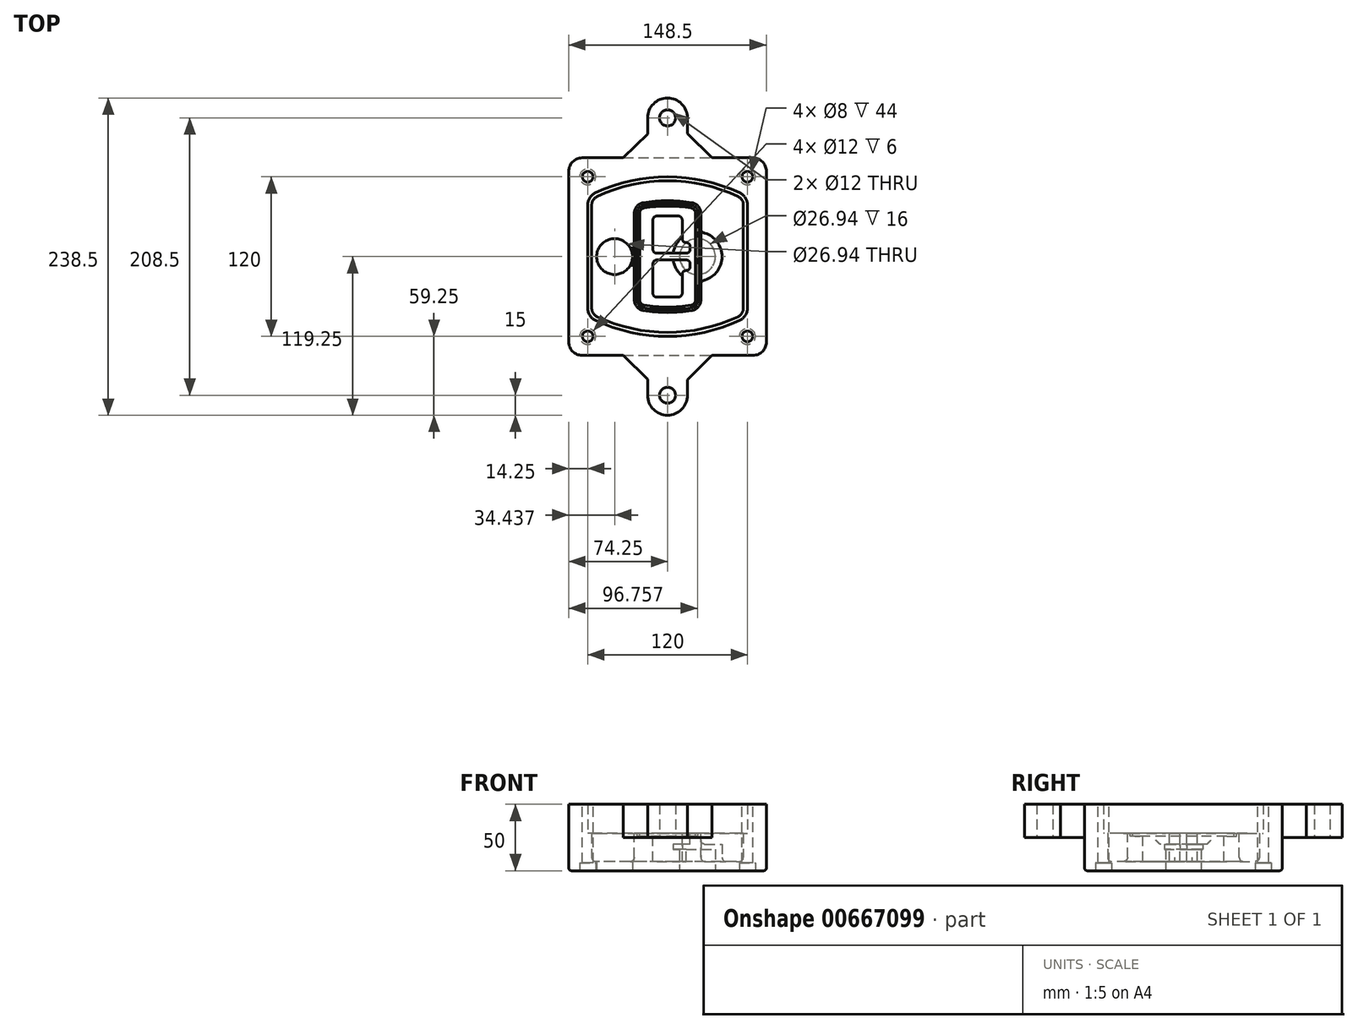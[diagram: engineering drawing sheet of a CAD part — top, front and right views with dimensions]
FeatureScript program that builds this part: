
annotation { "Feature Type Name" : "Feature", "Feature Type Description" : "" }
export const myFeature = defineFeature(function(context is Context, id is Id, definition is map)
    precondition{}
    {
        {
            var Q0;
            Q0=qCreatedBy(makeId("Top.planeOp"),FACE);
            var sketch = newSketch(context, id + "F0", { "sketchPlane" : qUnion([Q0])});
            skPoint(sketch, "E0.rect.middle", {"position": v(0, 0) * mm});
            skLineSegment(sketch, "E1.bottom", {"start": v(-64.25, -74.25) * mm, "end": v(64.25, -74.25) * mm});
            skLineSegment(sketch, "E1.top", {"start": v(-64.25, 74.25) * mm, "end": v(64.25, 74.25) * mm});
            skLineSegment(sketch, "E1.left", {"start": v(-74.25, -64.25) * mm, "end": v(-74.25, 64.25) * mm});
            skLineSegment(sketch, "E1.right", {"start": v(74.25, -64.25) * mm, "end": v(74.25, 64.25) * mm});
            skLineSegment(sketch, "E2", {"start": v(-74.25, 74.25) * mm, "end": v(74.25, -74.25) * mm, "construction": true});
            skLineSegment(sketch, "E3", {"start": v(74.25, 74.25) * mm, "end": v(-74.25, -74.25) * mm, "construction": true});
            skCircle(sketch, "E4", {"center": v(-60, 60) * mm, "radius": 4 * mm});
            skCircle(sketch, "E5", {"center": v(60, 60) * mm, "radius": 4 * mm});
            skCircle(sketch, "E6", {"center": v(60, -60) * mm, "radius": 4 * mm});
            skCircle(sketch, "E7", {"center": v(-60, -60) * mm, "radius": 4 * mm});
            skLineSegment(sketch, "E8", {"start": v(-60, 60) * mm, "end": v(60, 60) * mm, "construction": true});
            skLineSegment(sketch, "E9", {"start": v(60, 60) * mm, "end": v(60, -60) * mm, "construction": true});
            skLineSegment(sketch, "E10", {"start": v(60, -60) * mm, "end": v(-60, -60) * mm, "construction": true});
            skLineSegment(sketch, "E11", {"start": v(-60, -60) * mm, "end": v(-60, 60) * mm, "construction": true});
            skLineSegment(sketch, "E12", {"start": v(-60, 38.83) * mm, "end": v(-60, -38.83) * mm});
            skLineSegment(sketch, "E13", {"start": v(60, 38.83) * mm, "end": v(60, -38.83) * mm});
            skArc(sketch, "E14", {"start": v(54.26, 47.88) * mm, "mid": v(0, 60) * mm, "end": v(-54.26, 47.88) * mm});
            skArc(sketch, "E15", {"start": v(-54.26, -47.88) * mm, "mid": v(0, -60) * mm, "end": v(54.26, -47.88) * mm});
            skLineSegment(sketch, "E16", {"start": v(-60, 0) * mm, "end": v(60, 0) * mm, "construction": true});
            skPoint(sketch, "E17.visualSharp", {"position": v(-60, -45) * mm});
            skArc(sketch, "E17.filletArc", {"start": v(-60, -38.83) * mm, "mid": v(-58.44, -44.2) * mm, "end": v(-54.26, -47.88) * mm});
            skPoint(sketch, "E18.visualSharp", {"position": v(-60, 45) * mm});
            skArc(sketch, "E18.filletArc", {"start": v(-54.26, 47.88) * mm, "mid": v(-58.44, 44.2) * mm, "end": v(-60, 38.83) * mm});
            skPoint(sketch, "E19.visualSharp", {"position": v(60, 45) * mm});
            skArc(sketch, "E19.filletArc", {"start": v(60, 38.83) * mm, "mid": v(58.44, 44.2) * mm, "end": v(54.26, 47.88) * mm});
            skPoint(sketch, "E20.visualSharp", {"position": v(60, -45) * mm});
            skArc(sketch, "E20.filletArc", {"start": v(54.26, -47.88) * mm, "mid": v(58.44, -44.2) * mm, "end": v(60, -38.83) * mm});
            skPoint(sketch, "E21.visualSharp", {"position": v(-74.25, 74.25) * mm});
            skArc(sketch, "E21.filletArc", {"start": v(-64.25, 74.25) * mm, "mid": v(-71.32, 71.32) * mm, "end": v(-74.25, 64.25) * mm});
            skPoint(sketch, "E22.visualSharp", {"position": v(74.25, 74.25) * mm});
            skArc(sketch, "E22.filletArc", {"start": v(74.25, 64.25) * mm, "mid": v(71.32, 71.32) * mm, "end": v(64.25, 74.25) * mm});
            skPoint(sketch, "E23.visualSharp", {"position": v(74.25, -74.25) * mm});
            skArc(sketch, "E23.filletArc", {"start": v(64.25, -74.25) * mm, "mid": v(71.32, -71.32) * mm, "end": v(74.25, -64.25) * mm});
            skPoint(sketch, "E24.visualSharp", {"position": v(-74.25, -74.25) * mm});
            skArc(sketch, "E24.filletArc", {"start": v(-74.25, -64.25) * mm, "mid": v(-71.32, -71.32) * mm, "end": v(-64.25, -74.25) * mm});
            skArc(sketch, "E25.0", {"start": v(57, 38.83) * mm, "mid": v(55.9, 42.58) * mm, "end": v(52.98, 45.17) * mm});
            skLineSegment(sketch, "E25.1", {"start": v(57, 38.83) * mm, "end": v(57, -38.83) * mm});
            skArc(sketch, "E25.2", {"start": v(52.98, -45.17) * mm, "mid": v(55.9, -42.58) * mm, "end": v(57, -38.83) * mm});
            skArc(sketch, "E25.3", {"start": v(-52.98, -45.17) * mm, "mid": v(0, -57) * mm, "end": v(52.98, -45.17) * mm});
            skArc(sketch, "E25.4", {"start": v(-57, -38.83) * mm, "mid": v(-55.9, -42.58) * mm, "end": v(-52.98, -45.17) * mm});
            skArc(sketch, "E25.5", {"start": v(52.98, 45.17) * mm, "mid": v(0, 57) * mm, "end": v(-52.98, 45.17) * mm});
            skLineSegment(sketch, "E25.6", {"start": v(-57, 38.83) * mm, "end": v(-57, -38.83) * mm});
            skArc(sketch, "E25.7", {"start": v(-52.98, 45.17) * mm, "mid": v(-55.9, 42.58) * mm, "end": v(-57, 38.83) * mm});
            skArc(sketch, "E26.0", {"start": v(-55.96, 51.5) * mm, "mid": v(-61.82, 46.33) * mm, "end": v(-64, 38.83) * mm});
            skArc(sketch, "E26.1", {"start": v(55.96, 51.5) * mm, "mid": v(0, 64) * mm, "end": v(-55.96, 51.5) * mm});
            skArc(sketch, "E26.2", {"start": v(64, 38.83) * mm, "mid": v(61.82, 46.33) * mm, "end": v(55.96, 51.5) * mm});
            skLineSegment(sketch, "E26.3", {"start": v(64, 38.83) * mm, "end": v(64, -38.83) * mm});
            skArc(sketch, "E26.4", {"start": v(55.96, -51.5) * mm, "mid": v(61.82, -46.33) * mm, "end": v(64, -38.83) * mm});
            skLineSegment(sketch, "E26.5", {"start": v(-64, 38.83) * mm, "end": v(-64, -38.83) * mm});
            skArc(sketch, "E26.6", {"start": v(-55.96, -51.5) * mm, "mid": v(0, -64) * mm, "end": v(55.96, -51.5) * mm});
            skArc(sketch, "E26.7", {"start": v(-64, -38.83) * mm, "mid": v(-61.82, -46.33) * mm, "end": v(-55.96, -51.5) * mm});
            skSolve(sketch);
        }
        {
            var Q0;
            Q0=makeQuery(id+"F0.imprint","IMPRINT",FACE,{"disambiguationData":[TD([[makeQuery(id+"F0.imprint","IMPRINT",EDGE,{"derivedFrom":sQuery(id+"F0.wireOp",EDGE,"E1.bottom")}),1.0]])]});
            var Q1;
            Q1=makeQuery(id+"F0.imprint","IMPRINT",FACE,{"disambiguationData":[TD([[makeQuery(id+"F0.imprint","IMPRINT",EDGE,{"derivedFrom":sQuery(id+"F0.wireOp",EDGE,"E12")}),1.0]])]});
            var Q2;
            Q2=makeQuery(id+"F0.imprint","IMPRINT",FACE,{"disambiguationData":[TD([[makeQuery(id+"F0.imprint","IMPRINT",EDGE,{"derivedFrom":sQuery(id+"F0.wireOp",EDGE,"E25.0")}),1.0]])]});
            var Q3;
            Q3=makeQuery(id+"F0.imprint","IMPRINT",FACE,{"disambiguationData":[TD([[makeQuery(id+"F0.imprint","IMPRINT",EDGE,{"derivedFrom":sQuery(id+"F0.wireOp",EDGE,"E12")}),-1.0]])]});
            extrude(context, id + "F1", {"entities" : qUnion([Q0, Q1, Q2, Q3]), "oppositeDirection" : true, "depth" : 25 * mm});
        }
        {
            var Q0;
            Q0=makeQuery(id+"F0.imprint","IMPRINT",FACE,{"disambiguationData":[TD([[makeQuery(id+"F0.imprint","IMPRINT",EDGE,{"derivedFrom":sQuery(id+"F0.wireOp",EDGE,"E12")}),1.0]])]});
            extrude(context, id + "F2", {"entities" : qUnion([Q0]), "operationType" : NewBodyOperationType.ADD, "depth" : 3 * mm});
        }
        {
            var Q0;
            Q0=makeQuery(id+"F0.imprint","IMPRINT",FACE,{"disambiguationData":[TD([[makeQuery(id+"F0.imprint","IMPRINT",EDGE,{"derivedFrom":sQuery(id+"F0.wireOp",EDGE,"E25.0")}),1.0]])]});
            extrude(context, id + "F3", {"entities" : qUnion([Q0]), "operationType" : NewBodyOperationType.REMOVE, "oppositeDirection" : true, "depth" : 18 * mm});
        }
        {
            var Q0;
            Q0=makeQuery(id+"F2.opExtrude","CAP_FACE",FACE,{"disambiguationData":[OSD([sQuery(id+"F0.wireOp",EDGE,"E12"),sQuery(id+"F0.wireOp",EDGE,"E13"),sQuery(id+"F0.wireOp",EDGE,"E14"),sQuery(id+"F0.wireOp",EDGE,"E15"),sQuery(id+"F0.wireOp",EDGE,"E17.filletArc"),sQuery(id+"F0.wireOp",EDGE,"E18.filletArc"),sQuery(id+"F0.wireOp",EDGE,"E19.filletArc"),sQuery(id+"F0.wireOp",EDGE,"E20.filletArc"),sQuery(id+"F0.wireOp",EDGE,"E25.0"),sQuery(id+"F0.wireOp",EDGE,"E25.1"),sQuery(id+"F0.wireOp",EDGE,"E25.2"),sQuery(id+"F0.wireOp",EDGE,"E25.3"),sQuery(id+"F0.wireOp",EDGE,"E25.4"),sQuery(id+"F0.wireOp",EDGE,"E25.5"),sQuery(id+"F0.wireOp",EDGE,"E25.6"),sQuery(id+"F0.wireOp",EDGE,"E25.7")])],"isStart":false});
            var sketch = newSketch(context, id + "F4", { "sketchPlane" : qUnion([Q0])});
            skArc(sketch, "E27.0", {"start": v(-18.34, -40.45) * mm, "mid": v(0, -42) * mm, "end": v(18.34, -40.45) * mm});
            skArc(sketch, "E28.0", {"start": v(18.34, 40.45) * mm, "mid": v(0, 42) * mm, "end": v(-18.34, 40.45) * mm});
            skLineSegment(sketch, "E29", {"start": v(-25, 32.57) * mm, "end": v(-25, -32.57) * mm});
            skLineSegment(sketch, "E30", {"start": v(25, 32.57) * mm, "end": v(25, -32.57) * mm});
            skLineSegment(sketch, "E31", {"start": v(-25, 39.1) * mm, "end": v(25, 39.1) * mm, "construction": true});
            skLineSegment(sketch, "E32", {"start": v(-25, -39.1) * mm, "end": v(25, -39.1) * mm, "construction": true});
            skPoint(sketch, "E33.visualSharp", {"position": v(-25, 39.1) * mm});
            skArc(sketch, "E33.filletArc", {"start": v(-18.34, 40.45) * mm, "mid": v(-23.11, 37.73) * mm, "end": v(-25, 32.57) * mm});
            skPoint(sketch, "E34.visualSharp", {"position": v(25, 39.1) * mm});
            skArc(sketch, "E34.filletArc", {"start": v(25, 32.57) * mm, "mid": v(23.11, 37.73) * mm, "end": v(18.34, 40.45) * mm});
            skPoint(sketch, "E35.visualSharp", {"position": v(25, -39.1) * mm});
            skArc(sketch, "E35.filletArc", {"start": v(18.34, -40.45) * mm, "mid": v(23.11, -37.73) * mm, "end": v(25, -32.57) * mm});
            skPoint(sketch, "E36.visualSharp", {"position": v(-25, -39.1) * mm});
            skArc(sketch, "E36.filletArc", {"start": v(-25, -32.57) * mm, "mid": v(-23.11, -37.73) * mm, "end": v(-18.34, -40.45) * mm});
            skArc(sketch, "E37.0", {"start": v(52.98, 45.17) * mm, "mid": v(0, 57) * mm, "end": v(-52.98, 45.17) * mm});
            skArc(sketch, "E37.1", {"start": v(-52.98, 45.17) * mm, "mid": v(-55.9, 42.58) * mm, "end": v(-57, 38.83) * mm});
            skLineSegment(sketch, "E37.2", {"start": v(-57, 38.83) * mm, "end": v(-57, -38.83) * mm});
            skArc(sketch, "E37.3", {"start": v(-57, -38.83) * mm, "mid": v(-55.9, -42.58) * mm, "end": v(-52.98, -45.17) * mm});
            skArc(sketch, "E37.4", {"start": v(-52.98, -45.17) * mm, "mid": v(0, -57) * mm, "end": v(52.98, -45.17) * mm});
            skArc(sketch, "E37.5", {"start": v(52.98, -45.17) * mm, "mid": v(55.9, -42.58) * mm, "end": v(57, -38.83) * mm});
            skLineSegment(sketch, "E37.6", {"start": v(57, 38.83) * mm, "end": v(57, -38.83) * mm});
            skArc(sketch, "E37.7", {"start": v(57, 38.83) * mm, "mid": v(55.9, 42.58) * mm, "end": v(52.98, 45.17) * mm});
            skLineSegment(sketch, "E38.0", {"start": v(23, 32.57) * mm, "end": v(23, -32.57) * mm});
            skArc(sketch, "E38.1", {"start": v(18, -38.48) * mm, "mid": v(21.58, -36.44) * mm, "end": v(23, -32.57) * mm});
            skArc(sketch, "E38.2", {"start": v(-18, -38.48) * mm, "mid": v(0, -40) * mm, "end": v(18, -38.48) * mm});
            skArc(sketch, "E38.3", {"start": v(-23, -32.57) * mm, "mid": v(-21.58, -36.44) * mm, "end": v(-18, -38.48) * mm});
            skLineSegment(sketch, "E38.4", {"start": v(-23, 32.57) * mm, "end": v(-23, -32.57) * mm});
            skArc(sketch, "E38.5", {"start": v(23, 32.57) * mm, "mid": v(21.58, 36.44) * mm, "end": v(18, 38.48) * mm});
            skArc(sketch, "E38.6", {"start": v(-18, 38.48) * mm, "mid": v(-21.58, 36.44) * mm, "end": v(-23, 32.57) * mm});
            skArc(sketch, "E38.7", {"start": v(18, 38.48) * mm, "mid": v(0, 40) * mm, "end": v(-18, 38.48) * mm});
            skArc(sketch, "E39.0", {"start": v(21, 32.57) * mm, "mid": v(20.06, 35.15) * mm, "end": v(17.67, 36.5) * mm});
            skLineSegment(sketch, "E39.1", {"start": v(21, 32.57) * mm, "end": v(21, -32.57) * mm});
            skArc(sketch, "E39.2", {"start": v(17.67, -36.5) * mm, "mid": v(20.06, -35.15) * mm, "end": v(21, -32.57) * mm});
            skArc(sketch, "E39.3", {"start": v(-17.67, -36.5) * mm, "mid": v(0, -38) * mm, "end": v(17.67, -36.5) * mm});
            skArc(sketch, "E39.4", {"start": v(-21, -32.57) * mm, "mid": v(-20.06, -35.15) * mm, "end": v(-17.67, -36.5) * mm});
            skArc(sketch, "E39.5", {"start": v(17.67, 36.5) * mm, "mid": v(0, 38) * mm, "end": v(-17.67, 36.5) * mm});
            skLineSegment(sketch, "E39.6", {"start": v(-21, 32.57) * mm, "end": v(-21, -32.57) * mm});
            skArc(sketch, "E39.7", {"start": v(-17.67, 36.5) * mm, "mid": v(-20.06, 35.15) * mm, "end": v(-21, 32.57) * mm});
            skLineSegment(sketch, "E40", {"start": v(-25, 0) * mm, "end": v(25, 0) * mm, "construction": true});
            skLineSegment(sketch, "E41", {"start": v(-11, 5.5) * mm, "end": v(-11, 27.5) * mm});
            skLineSegment(sketch, "E42", {"start": v(-8, 30.5) * mm, "end": v(8, 30.5) * mm});
            skLineSegment(sketch, "E43", {"start": v(11, 27.5) * mm, "end": v(11, 13.5) * mm});
            skLineSegment(sketch, "E44", {"start": v(14, 10.5) * mm, "end": v(14, 10.5) * mm});
            skLineSegment(sketch, "E45", {"start": v(17, 7.5) * mm, "end": v(17, 5.5) * mm});
            skLineSegment(sketch, "E46", {"start": v(14, 2.5) * mm, "end": v(-8, 2.5) * mm});
            skPoint(sketch, "E47.visualSharp", {"position": v(-11, 30.5) * mm});
            skArc(sketch, "E47.filletArc", {"start": v(-8, 30.5) * mm, "mid": v(-10.12, 29.62) * mm, "end": v(-11, 27.5) * mm});
            skPoint(sketch, "E48.visualSharp", {"position": v(11, 30.5) * mm});
            skArc(sketch, "E48.filletArc", {"start": v(11, 27.5) * mm, "mid": v(10.12, 29.62) * mm, "end": v(8, 30.5) * mm});
            skPoint(sketch, "E49.visualSharp", {"position": v(11, 10.5) * mm});
            skArc(sketch, "E49.filletArc", {"start": v(11, 13.5) * mm, "mid": v(11.88, 11.38) * mm, "end": v(14, 10.5) * mm});
            skPoint(sketch, "E50.visualSharp", {"position": v(17, 10.5) * mm});
            skArc(sketch, "E50.filletArc", {"start": v(17, 7.5) * mm, "mid": v(16.12, 9.62) * mm, "end": v(14, 10.5) * mm});
            skPoint(sketch, "E51.visualSharp", {"position": v(17, 2.5) * mm});
            skArc(sketch, "E51.filletArc", {"start": v(14, 2.5) * mm, "mid": v(16.12, 3.38) * mm, "end": v(17, 5.5) * mm});
            skPoint(sketch, "E52.visualSharp", {"position": v(-11, 2.5) * mm});
            skArc(sketch, "E52.filletArc", {"start": v(-11, 5.5) * mm, "mid": v(-10.12, 3.38) * mm, "end": v(-8, 2.5) * mm});
            skLineSegment(sketch, "E53.0.MirrorCS", {"start": v(14, -2.5) * mm, "end": v(-8, -2.5) * mm});
            skArc(sketch, "E54.0.MirrorCS", {"start": v(-11, -5.5) * mm, "mid": v(-10.12, -3.38) * mm, "end": v(-8, -2.5) * mm});
            skLineSegment(sketch, "E55.0.MirrorCS", {"start": v(-11, -5.5) * mm, "end": v(-11, -27.5) * mm});
            skArc(sketch, "E56.0.MirrorCS", {"start": v(-8, -30.5) * mm, "mid": v(-10.12, -29.62) * mm, "end": v(-11, -27.5) * mm});
            skLineSegment(sketch, "E57.0.MirrorCS", {"start": v(-8, -30.5) * mm, "end": v(8, -30.5) * mm});
            skArc(sketch, "E58.0.MirrorCS", {"start": v(11, -27.5) * mm, "mid": v(10.12, -29.62) * mm, "end": v(8, -30.5) * mm});
            skLineSegment(sketch, "E59.0.MirrorCS", {"start": v(11, -27.5) * mm, "end": v(11, -13.5) * mm});
            skArc(sketch, "E60.0.MirrorCS", {"start": v(11, -13.5) * mm, "mid": v(11.88, -11.38) * mm, "end": v(14, -10.5) * mm});
            skArc(sketch, "E61.0.MirrorCS", {"start": v(17, -7.5) * mm, "mid": v(16.12, -9.62) * mm, "end": v(14, -10.5) * mm});
            skLineSegment(sketch, "E62.0.MirrorCS", {"start": v(17, -7.5) * mm, "end": v(17, -5.5) * mm});
            skArc(sketch, "E63.0.MirrorCS", {"start": v(14, -2.5) * mm, "mid": v(16.12, -3.38) * mm, "end": v(17, -5.5) * mm});
            skSolve(sketch);
        }
        {
            var Q0;
            Q0=makeQuery(id+"F4.imprint","IMPRINT",FACE,{"disambiguationData":[TD([[makeQuery(id+"F4.imprint","IMPRINT",EDGE,{"derivedFrom":sQuery(id+"F4.wireOp",EDGE,"E27.0")}),1.0]])]});
            var Q1;
            Q1=makeQuery(id+"F4.imprint","IMPRINT",FACE,{"disambiguationData":[TD([[makeQuery(id+"F4.imprint","IMPRINT",EDGE,{"derivedFrom":sQuery(id+"F4.wireOp",EDGE,"E38.0")}),-1.0]])]});
            var Q2;
            Q2=makeQuery(id+"F4.imprint","IMPRINT",FACE,{"disambiguationData":[TD([[makeQuery(id+"F4.imprint","IMPRINT",EDGE,{"derivedFrom":sQuery(id+"F4.wireOp",EDGE,"E39.0")}),1.0]])]});
            extrude(context, id + "F5", {"entities" : qUnion([Q0, Q1, Q2]), "operationType" : NewBodyOperationType.ADD, "endBound" : BoundingType.UP_TO_NEXT, "oppositeDirection" : true, "depth" : 25 * mm});
        }
        {
            var Q0;
            Q0=makeQuery(id+"F4.imprint","IMPRINT",FACE,{"disambiguationData":[TD([[makeQuery(id+"F4.imprint","IMPRINT",EDGE,{"derivedFrom":sQuery(id+"F4.wireOp",EDGE,"E38.0")}),-1.0]])]});
            extrude(context, id + "F6", {"entities" : qUnion([Q0]), "operationType" : NewBodyOperationType.REMOVE, "oppositeDirection" : true, "depth" : 2 * mm});
        }
        {
            var Q0;
            Q0=makeQuery(id+"F1.opExtrude","CAP_FACE",FACE,{"disambiguationData":[OSD([sQuery(id+"F0.wireOp",EDGE,"E1.bottom"),sQuery(id+"F0.wireOp",EDGE,"E1.top"),sQuery(id+"F0.wireOp",EDGE,"E1.left"),sQuery(id+"F0.wireOp",EDGE,"E1.right"),sQuery(id+"F0.wireOp",EDGE,"E4"),sQuery(id+"F0.wireOp",EDGE,"E5"),sQuery(id+"F0.wireOp",EDGE,"E6"),sQuery(id+"F0.wireOp",EDGE,"E7"),sQuery(id+"F0.wireOp",EDGE,"E21.filletArc"),sQuery(id+"F0.wireOp",EDGE,"E22.filletArc"),sQuery(id+"F0.wireOp",EDGE,"E23.filletArc"),sQuery(id+"F0.wireOp",EDGE,"E24.filletArc")])],"isStart":false});
            var sketch = newSketch(context, id + "F7", { "sketchPlane" : qUnion([Q0])});
            skCircle(sketch, "E64", {"center": v(22.5, 0) * mm, "radius": 13.47 * mm});
            skCircle(sketch, "E65", {"center": v(-39.81, 0) * mm, "radius": 13.47 * mm});
            skLineSegment(sketch, "E66", {"start": v(74.25, 0) * mm, "end": v(-74.25, 0) * mm});
            skCircle(sketch, "E67", {"center": v(22.5, 0) * mm, "radius": 18.47 * mm});
            skCircle(sketch, "E68", {"center": v(60, -60) * mm, "radius": 6 * mm});
            skCircle(sketch, "E69", {"center": v(-60, -60) * mm, "radius": 6 * mm});
            skCircle(sketch, "E70", {"center": v(-60, 60) * mm, "radius": 6 * mm});
            skCircle(sketch, "E71", {"center": v(60, 60) * mm, "radius": 6 * mm});
            skSolve(sketch);
        }
        {
            var Q0;
            {var subQ1=sQuery(id+"F7.wireOp",EDGE,"E66");var subQ4=sQuery(id+"F7.wireOp",EDGE,"E64");var subQ6=makeQuery(id+"F7.imprint","INTERSECT",VERTEX,{"disambiguationData":[OD(0.0)],"derivedFrom":[subQ4,subQ1]});Q0=makeQuery(id+"F7.imprint","IMPRINT",FACE,{"disambiguationData":[TD([[makeQuery(id+"F7.imprint","IMPRINT",EDGE,{"disambiguationData":[TD([[subQ6,-1.0]])],"derivedFrom":subQ4}),-1.0]])]});}
            var Q1;
            {var subQ0=sQuery(id+"F7.wireOp",EDGE,"E66");var subQ1=sQuery(id+"F7.wireOp",EDGE,"E64");var subQ3=makeQuery(id+"F7.imprint","INTERSECT",VERTEX,{"disambiguationData":[OD(0.0)],"derivedFrom":[subQ1,subQ0]});Q1=makeQuery(id+"F7.imprint","IMPRINT",FACE,{"disambiguationData":[TD([[makeQuery(id+"F7.imprint","IMPRINT",EDGE,{"disambiguationData":[TD([[subQ3,-1.0]])],"derivedFrom":subQ1}),1.0]])]});}
            var Q2;
            {var subQ0=sQuery(id+"F7.wireOp",EDGE,"E66");var subQ1=sQuery(id+"F7.wireOp",EDGE,"E64");var subQ3=makeQuery(id+"F7.imprint","INTERSECT",VERTEX,{"disambiguationData":[OD(0.0)],"derivedFrom":[subQ1,subQ0]});Q2=makeQuery(id+"F7.imprint","IMPRINT",FACE,{"disambiguationData":[TD([[makeQuery(id+"F7.imprint","IMPRINT",EDGE,{"disambiguationData":[TD([[subQ3,1.0]])],"derivedFrom":subQ1}),1.0]])]});}
            var Q3;
            {var subQ1=sQuery(id+"F7.wireOp",EDGE,"E66");var subQ4=sQuery(id+"F7.wireOp",EDGE,"E64");var subQ6=makeQuery(id+"F7.imprint","INTERSECT",VERTEX,{"disambiguationData":[OD(0.0)],"derivedFrom":[subQ4,subQ1]});Q3=makeQuery(id+"F7.imprint","IMPRINT",FACE,{"disambiguationData":[TD([[makeQuery(id+"F7.imprint","IMPRINT",EDGE,{"disambiguationData":[TD([[subQ6,1.0]])],"derivedFrom":subQ4}),-1.0]])]});}
            extrude(context, id + "F8", {"entities" : qUnion([Q0, Q1, Q2, Q3]), "operationType" : NewBodyOperationType.ADD, "oppositeDirection" : true, "depth" : 20 * mm});
        }
        {
            var Q0;
            {var subQ0=sQuery(id+"F7.wireOp",EDGE,"E66");var subQ1=sQuery(id+"F7.wireOp",EDGE,"E64");var subQ3=makeQuery(id+"F7.imprint","INTERSECT",VERTEX,{"disambiguationData":[OD(0.0)],"derivedFrom":[subQ1,subQ0]});Q0=makeQuery(id+"F7.imprint","IMPRINT",FACE,{"disambiguationData":[TD([[makeQuery(id+"F7.imprint","IMPRINT",EDGE,{"disambiguationData":[TD([[subQ3,-1.0]])],"derivedFrom":subQ1}),1.0]])]});}
            var Q1;
            {var subQ0=sQuery(id+"F7.wireOp",EDGE,"E66");var subQ1=sQuery(id+"F7.wireOp",EDGE,"E64");var subQ3=makeQuery(id+"F7.imprint","INTERSECT",VERTEX,{"disambiguationData":[OD(0.0)],"derivedFrom":[subQ1,subQ0]});Q1=makeQuery(id+"F7.imprint","IMPRINT",FACE,{"disambiguationData":[TD([[makeQuery(id+"F7.imprint","IMPRINT",EDGE,{"disambiguationData":[TD([[subQ3,1.0]])],"derivedFrom":subQ1}),1.0]])]});}
            extrude(context, id + "F9", {"entities" : qUnion([Q0, Q1]), "operationType" : NewBodyOperationType.REMOVE, "oppositeDirection" : true, "depth" : 16 * mm});
        }
        {
            var Q0;
            {var subQ0=sQuery(id+"F7.wireOp",EDGE,"E66");var subQ1=sQuery(id+"F7.wireOp",EDGE,"E65");var subQ3=makeQuery(id+"F7.imprint","INTERSECT",VERTEX,{"disambiguationData":[OD(0.0)],"derivedFrom":[subQ1,subQ0]});Q0=makeQuery(id+"F7.imprint","IMPRINT",FACE,{"disambiguationData":[TD([[makeQuery(id+"F7.imprint","IMPRINT",EDGE,{"disambiguationData":[TD([[subQ3,-1.0]])],"derivedFrom":subQ1}),1.0]])]});}
            var Q1;
            {var subQ0=sQuery(id+"F7.wireOp",EDGE,"E66");var subQ1=sQuery(id+"F7.wireOp",EDGE,"E65");var subQ3=makeQuery(id+"F7.imprint","INTERSECT",VERTEX,{"disambiguationData":[OD(0.0)],"derivedFrom":[subQ1,subQ0]});Q1=makeQuery(id+"F7.imprint","IMPRINT",FACE,{"disambiguationData":[TD([[makeQuery(id+"F7.imprint","IMPRINT",EDGE,{"disambiguationData":[TD([[subQ3,1.0]])],"derivedFrom":subQ1}),1.0]])]});}
            extrude(context, id + "F10", {"entities" : qUnion([Q0, Q1]), "operationType" : NewBodyOperationType.REMOVE, "oppositeDirection" : true, "depth" : 25 * mm});
        }
        {
            var Q0;
            Q0=makeQuery(id+"F7.imprint","IMPRINT",FACE,{"disambiguationData":[TD([[makeQuery(id+"F7.imprint","IMPRINT",EDGE,{"derivedFrom":sQuery(id+"F7.wireOp",EDGE,"E68")}),1.0]])]});
            var Q1;
            Q1=makeQuery(id+"F7.imprint","IMPRINT",FACE,{"disambiguationData":[TD([[makeQuery(id+"F7.imprint","IMPRINT",EDGE,{"derivedFrom":makeQuery(id+"F1.opExtrude","CAP_EDGE",EDGE,{"disambiguationData":[OSD([sQuery(id+"F0.wireOp",EDGE,"E5")])],"isStart":false})}),-1.0]])]});
            var Q2;
            Q2=makeQuery(id+"F7.imprint","IMPRINT",FACE,{"disambiguationData":[TD([[makeQuery(id+"F7.imprint","IMPRINT",EDGE,{"derivedFrom":sQuery(id+"F7.wireOp",EDGE,"E69")}),1.0]])]});
            var Q3;
            Q3=makeQuery(id+"F7.imprint","IMPRINT",FACE,{"disambiguationData":[TD([[makeQuery(id+"F7.imprint","IMPRINT",EDGE,{"derivedFrom":makeQuery(id+"F1.opExtrude","CAP_EDGE",EDGE,{"disambiguationData":[OSD([sQuery(id+"F0.wireOp",EDGE,"E4")])],"isStart":false})}),-1.0]])]});
            var Q4;
            Q4=makeQuery(id+"F7.imprint","IMPRINT",FACE,{"disambiguationData":[TD([[makeQuery(id+"F7.imprint","IMPRINT",EDGE,{"derivedFrom":sQuery(id+"F7.wireOp",EDGE,"E70")}),1.0]])]});
            var Q5;
            Q5=makeQuery(id+"F7.imprint","IMPRINT",FACE,{"disambiguationData":[TD([[makeQuery(id+"F7.imprint","IMPRINT",EDGE,{"derivedFrom":makeQuery(id+"F1.opExtrude","CAP_EDGE",EDGE,{"disambiguationData":[OSD([sQuery(id+"F0.wireOp",EDGE,"E7")])],"isStart":false})}),-1.0]])]});
            var Q6;
            Q6=makeQuery(id+"F7.imprint","IMPRINT",FACE,{"disambiguationData":[TD([[makeQuery(id+"F7.imprint","IMPRINT",EDGE,{"derivedFrom":sQuery(id+"F7.wireOp",EDGE,"E71")}),1.0]])]});
            var Q7;
            Q7=makeQuery(id+"F7.imprint","IMPRINT",FACE,{"disambiguationData":[TD([[makeQuery(id+"F7.imprint","IMPRINT",EDGE,{"derivedFrom":makeQuery(id+"F1.opExtrude","CAP_EDGE",EDGE,{"disambiguationData":[OSD([sQuery(id+"F0.wireOp",EDGE,"E6")])],"isStart":false})}),-1.0]])]});
            extrude(context, id + "F11", {"entities" : qUnion([Q0, Q1, Q2, Q3, Q4, Q5, Q6, Q7]), "operationType" : NewBodyOperationType.REMOVE, "oppositeDirection" : true, "depth" : 6 * mm});
        }
        {
            var Q0;
            Q0=makeQuery(id+"F9.boolean.opBoolean","COPY",FACE,{"derivedFrom":makeQuery(id+"F9.opExtrude","CAP_FACE",FACE,{"disambiguationData":[OSD([sQuery(id+"F7.wireOp",EDGE,"E64")])],"isStart":false})});
            var sketch = newSketch(context, id + "F12", { "sketchPlane" : qUnion([Q0])});
            skArc(sketch, "E72.0", {"start": v(11, 14.45) * mm, "mid": v(6.45, 9.13) * mm, "end": v(4.2, 2.5) * mm});
            skArc(sketch, "E72.1", {"start": v(4.2, -2.5) * mm, "mid": v(6.45, -9.13) * mm, "end": v(11, -14.45) * mm});
            skLineSegment(sketch, "E73", {"start": v(4.2, -2.5) * mm, "end": v(14, -2.5) * mm});
            skLineSegment(sketch, "E74.0", {"start": v(14, 2.5) * mm, "end": v(4.2, 2.5) * mm});
            skArc(sketch, "E74.1", {"start": v(14, 2.5) * mm, "mid": v(16.12, 3.38) * mm, "end": v(17, 5.5) * mm});
            skLineSegment(sketch, "E74.2", {"start": v(17, 7.5) * mm, "end": v(17, 5.5) * mm});
            skArc(sketch, "E74.3", {"start": v(17, 7.5) * mm, "mid": v(16.12, 9.62) * mm, "end": v(14, 10.5) * mm});
            skArc(sketch, "E74.4", {"start": v(11, 13.5) * mm, "mid": v(11.88, 11.38) * mm, "end": v(14, 10.5) * mm});
            skLineSegment(sketch, "E74.5", {"start": v(11, 14.45) * mm, "end": v(11, 13.5) * mm});
            skLineSegment(sketch, "E74.7", {"start": v(14, -2.5) * mm, "end": v(4.2, -2.5) * mm});
            skArc(sketch, "E74.8", {"start": v(14, -2.5) * mm, "mid": v(16.12, -3.38) * mm, "end": v(17, -5.5) * mm});
            skLineSegment(sketch, "E74.9", {"start": v(17, -7.5) * mm, "end": v(17, -5.5) * mm});
            skArc(sketch, "E74.10", {"start": v(17, -7.5) * mm, "mid": v(16.12, -9.62) * mm, "end": v(14, -10.5) * mm});
            skArc(sketch, "E74.11", {"start": v(11, -13.5) * mm, "mid": v(11.88, -11.38) * mm, "end": v(14, -10.5) * mm});
            skLineSegment(sketch, "E74.12", {"start": v(11, -14.45) * mm, "end": v(11, -13.5) * mm});
            skPoint(sketch, "E75.orphan", {"position": v(11, -27.5) * mm});
            skPoint(sketch, "E76.orphan", {"position": v(-8, -2.5) * mm});
            skPoint(sketch, "E77.orphan", {"position": v(-8, 2.5) * mm});
            skPoint(sketch, "E78.orphan", {"position": v(11, 27.5) * mm});
            skSolve(sketch);
        }
        {
            var Q0;
            {var subQ7=sQuery(id+"F12.wireOp",EDGE,"E72.0");var subQ14=sQuery(id+"F12.wireOp",EDGE,"E72.1");var subQ16=sQuery(id+"F12.wireOp",EDGE,"E74.1");var subQ18=sQuery(id+"F12.wireOp",EDGE,"E74.8");Q0=qUnion([makeQuery(id+"F12.imprint","IMPRINT",FACE,{"disambiguationData":[TD([[makeQuery(id+"F12.imprint","IMPRINT",EDGE,{"derivedFrom":subQ7}),1.0]])]}),makeQuery(id+"F12.imprint","IMPRINT",FACE,{"disambiguationData":[TD([[makeQuery(id+"F12.imprint","IMPRINT",EDGE,{"derivedFrom":subQ14}),1.0]])]}),makeQuery(id+"F12.imprint","IMPRINT",FACE,{"disambiguationData":[TD([[makeQuery(id+"F12.imprint","IMPRINT",EDGE,{"derivedFrom":subQ16}),1.0]])]}),makeQuery(id+"F12.imprint","IMPRINT",FACE,{"disambiguationData":[TD([[makeQuery(id+"F12.imprint","IMPRINT",EDGE,{"derivedFrom":subQ18}),-1.0]])]})]);}
            var Q1;
            Q1=makeQuery(id+"F5.boolean.opBoolean","SPLIT",FACE,{"disambiguationData":[TD([makeQuery(id+"F5.opExtrude","SWEPT_FACE",FACE,{"disambiguationData":[OSD([sQuery(id+"F4.wireOp",EDGE,"E41")])]})])],"derivedFrom":makeQuery(id+"F3.boolean.opBoolean","COPY",FACE,{"derivedFrom":makeQuery(id+"F3.opExtrude","CAP_FACE",FACE,{"disambiguationData":[OSD([sQuery(id+"F0.wireOp",EDGE,"E25.0"),sQuery(id+"F0.wireOp",EDGE,"E25.1"),sQuery(id+"F0.wireOp",EDGE,"E25.2"),sQuery(id+"F0.wireOp",EDGE,"E25.3"),sQuery(id+"F0.wireOp",EDGE,"E25.4"),sQuery(id+"F0.wireOp",EDGE,"E25.5"),sQuery(id+"F0.wireOp",EDGE,"E25.6"),sQuery(id+"F0.wireOp",EDGE,"E25.7")])],"isStart":false})})});
            extrude(context, id + "F13", {"entities" : qUnion([Q0]), "operationType" : NewBodyOperationType.REMOVE, "endBound" : BoundingType.UP_TO_SURFACE, "endBoundEntityFace" : qUnion([Q1]), "depth" : 25 * mm});
        }
        {
            var Q0;
            Q0=makeQuery(id+"F3.boolean.opBoolean","COPY",EDGE,{"derivedFrom":makeQuery(id+"F3.opExtrude","CAP_EDGE",EDGE,{"disambiguationData":[OSD([sQuery(id+"F0.wireOp",EDGE,"E25.6")])],"isStart":false})});
            var Q1;
            Q1=makeQuery(id+"F8.boolean.opBoolean","INTERSECT",EDGE,{"derivedFrom":[makeQuery(id+"F5.opExtrude","SWEPT_FACE",FACE,{"disambiguationData":[OSD([sQuery(id+"F4.wireOp",EDGE,"E30")])]}),makeQuery(id+"F8.opExtrude","CAP_FACE",FACE,{"disambiguationData":[OSD([sQuery(id+"F7.wireOp",EDGE,"E67")])],"isStart":false})]});
            var Q2;
            Q2=makeQuery(id+"F8.boolean.opBoolean","INTERSECT",EDGE,{"disambiguationData":[OD(1.0)],"derivedFrom":[makeQuery(id+"F5.opExtrude","SWEPT_FACE",FACE,{"disambiguationData":[OSD([sQuery(id+"F4.wireOp",EDGE,"E30")])]}),makeQuery(id+"F8.opExtrude","SWEPT_FACE",FACE,{"disambiguationData":[OSD([sQuery(id+"F7.wireOp",EDGE,"E67")])]})]});
            var Q3;
            {var subQ0=sQuery(id+"F4.wireOp",EDGE,"E30");Q3=makeQuery(id+"F8.boolean.opBoolean","SPLIT",EDGE,{"disambiguationData":[TD([makeQuery(id+"F5.opExtrude","SWEPT_FACE",FACE,{"disambiguationData":[OSD([sQuery(id+"F4.wireOp",EDGE,"E35.filletArc")])]})])],"derivedFrom":makeQuery(id+"F5.opExtrude","CAP_EDGE",EDGE,{"disambiguationData":[OSD([subQ0])],"isStart":false})});}
            var Q4;
            {var subQ0=sQuery(id+"F0.wireOp",EDGE,"E25.7");var subQ1=sQuery(id+"F0.wireOp",EDGE,"E25.1");var subQ2=sQuery(id+"F0.wireOp",EDGE,"E25.6");var subQ3=sQuery(id+"F0.wireOp",EDGE,"E25.5");var subQ4=sQuery(id+"F0.wireOp",EDGE,"E25.4");var subQ5=sQuery(id+"F0.wireOp",EDGE,"E25.0");var subQ6=sQuery(id+"F0.wireOp",EDGE,"E25.2");var subQ7=sQuery(id+"F0.wireOp",EDGE,"E25.3");Q4=makeQuery(id+"F8.boolean.opBoolean","INTERSECT",EDGE,{"derivedFrom":[makeQuery(id+"F5.boolean.opBoolean","SPLIT",FACE,{"disambiguationData":[TD([makeQuery(id+"F2.opExtrude","SWEPT_FACE",FACE,{"disambiguationData":[OSD([subQ5])]})])],"derivedFrom":makeQuery(id+"F3.boolean.opBoolean","COPY",FACE,{"derivedFrom":makeQuery(id+"F3.opExtrude","CAP_FACE",FACE,{"disambiguationData":[OSD([subQ5,subQ1,subQ6,subQ7,subQ4,subQ3,subQ2,subQ0])],"isStart":false})})}),makeQuery(id+"F8.opExtrude","SWEPT_FACE",FACE,{"disambiguationData":[OSD([sQuery(id+"F7.wireOp",EDGE,"E67")])]})]});}
            var Q5;
            Q5=makeQuery(id+"F8.boolean.opBoolean","INTERSECT",EDGE,{"disambiguationData":[OD(0.0)],"derivedFrom":[makeQuery(id+"F5.opExtrude","SWEPT_FACE",FACE,{"disambiguationData":[OSD([sQuery(id+"F4.wireOp",EDGE,"E30")])]}),makeQuery(id+"F8.opExtrude","SWEPT_FACE",FACE,{"disambiguationData":[OSD([sQuery(id+"F7.wireOp",EDGE,"E67")])]})]});
            fillet(context, id + "F14", {"entities" : qUnion([Q0, Q1, Q2, Q3, Q4, Q5]), "radius" : 3 * mm, "tangentPropagation" : true, "allowEdgeOverflow" : false});
        }
        {
            var Q0;
            Q0=makeQuery(id+"F1.opExtrude","CAP_EDGE",EDGE,{"disambiguationData":[OSD([sQuery(id+"F0.wireOp",EDGE,"E1.bottom")])],"isStart":false});
            fillet(context, id + "F15", {"entities" : qUnion([Q0]), "radius" : 2 * mm, "tangentPropagation" : true, "allowEdgeOverflow" : false});
        }
        {
            var Q0;
            {var subQ0=sQuery(id+"F0.wireOp",EDGE,"E21.filletArc");var subQ1=sQuery(id+"F0.wireOp",EDGE,"E7");var subQ2=sQuery(id+"F0.wireOp",EDGE,"E6");var subQ3=sQuery(id+"F0.wireOp",EDGE,"E5");var subQ4=sQuery(id+"F0.wireOp",EDGE,"E4");var subQ5=sQuery(id+"F0.wireOp",EDGE,"E22.filletArc");var subQ6=sQuery(id+"F0.wireOp",EDGE,"E1.bottom");var subQ7=sQuery(id+"F0.wireOp",EDGE,"E1.right");var subQ8=sQuery(id+"F0.wireOp",EDGE,"E1.top");var subQ9=sQuery(id+"F0.wireOp",EDGE,"E1.left");var subQ10=sQuery(id+"F0.wireOp",EDGE,"E23.filletArc");var subQ11=sQuery(id+"F0.wireOp",EDGE,"E24.filletArc");Q0=makeQuery(id+"F2.boolean.opBoolean","SPLIT",FACE,{"disambiguationData":[TD([makeQuery(id+"F1.opExtrude","SWEPT_FACE",FACE,{"disambiguationData":[OSD([subQ6])]})])],"derivedFrom":makeQuery(id+"F1.opExtrude","CAP_FACE",FACE,{"disambiguationData":[OSD([subQ6,subQ8,subQ9,subQ7,subQ4,subQ3,subQ2,subQ1,subQ0,subQ5,subQ10,subQ11])],"isStart":true})});}
            var sketch = newSketch(context, id + "F16", { "sketchPlane" : qUnion([Q0])});
            skLineSegment(sketch, "E79", {"start": v(-15, 92.25) * mm, "end": v(-15, 104.25) * mm});
            skLineSegment(sketch, "E80", {"start": v(15, 92.5) * mm, "end": v(15, 104.25) * mm});
            skArc(sketch, "E81", {"start": v(15, 104.25) * mm, "mid": v(0, 119.25) * mm, "end": v(-15, 104.25) * mm});
            skCircle(sketch, "E82", {"center": v(0, 104.25) * mm, "radius": 6 * mm});
            skLineSegment(sketch, "E83", {"start": v(-15, 92.25) * mm, "end": v(-33.34, 74.25) * mm});
            skLineSegment(sketch, "E84", {"start": v(15, 92.5) * mm, "end": v(33.25, 74.25) * mm});
            skLineSegment(sketch, "E85", {"start": v(-74.25, 0) * mm, "end": v(74.25, 0) * mm, "construction": true});
            skLineSegment(sketch, "E86.MirrorCS", {"start": v(15, -92.5) * mm, "end": v(15, -104.25) * mm});
            skLineSegment(sketch, "E87.MirrorCS", {"start": v(-15, -92.25) * mm, "end": v(-15, -104.25) * mm});
            skArc(sketch, "E88.MirrorCS", {"start": v(15, -104.25) * mm, "mid": v(0, -119.25) * mm, "end": v(-15, -104.25) * mm});
            skCircle(sketch, "E89.MirrorC", {"center": v(0, -104.25) * mm, "radius": 6 * mm});
            skLineSegment(sketch, "E90.MirrorCS", {"start": v(0, -104.25) * mm, "end": v(0, -76.57) * mm});
            skLineSegment(sketch, "E91.MirrorCS", {"start": v(15, -92.5) * mm, "end": v(15, -104.25) * mm, "construction": true});
            skLineSegment(sketch, "E92.MirrorCS", {"start": v(0, -104.25) * mm, "end": v(0, -76.57) * mm, "construction": true});
            skLineSegment(sketch, "E93.MirrorCS", {"start": v(15, -92.5) * mm, "end": v(33.25, -74.25) * mm});
            skLineSegment(sketch, "E94.MirrorCS", {"start": v(-15, -92.25) * mm, "end": v(-15, -104.25) * mm, "construction": true});
            skLineSegment(sketch, "E95.MirrorCS", {"start": v(-15, -92.25) * mm, "end": v(-33.34, -74.25) * mm});
            skCircle(sketch, "E96.MirrorC", {"center": v(0, -104.25) * mm, "radius": 6 * mm, "construction": true});
            skArc(sketch, "E97.MirrorCS", {"start": v(15, -104.25) * mm, "mid": v(0, -119.25) * mm, "end": v(-15, -104.25) * mm, "construction": true});
            skLineSegment(sketch, "E98", {"start": v(0, 74.25) * mm, "end": v(0, 104.25) * mm, "construction": true});
            skSolve(sketch);
        }
        {
            var Q0;
            Q0=makeQuery(id+"F16.imprint","IMPRINT",FACE,{"disambiguationData":[TD([[makeQuery(id+"F16.imprint","IMPRINT",EDGE,{"derivedFrom":sQuery(id+"F16.wireOp",EDGE,"E79")}),-1.0]])]});
            var Q1;
            Q1=makeQuery(id+"F16.imprint","IMPRINT",FACE,{"disambiguationData":[TD([[makeQuery(id+"F16.imprint","IMPRINT",EDGE,{"derivedFrom":sQuery(id+"F16.wireOp",EDGE,"E86.MirrorCS")}),-1.0]])]});
            var Q2;
            Q2=makeQuery(id+"F16.imprint","IMPRINT",FACE,{"disambiguationData":[TD([[makeQuery(id+"F16.imprint","IMPRINT",EDGE,{"derivedFrom":makeQuery(id+"F1.opExtrude","CAP_EDGE",EDGE,{"disambiguationData":[OSD([sQuery(id+"F0.wireOp",EDGE,"E1.left")])],"isStart":true})}),-1.0]])]});
            extrude(context, id + "F17", {"entities" : qUnion([Q0, Q1, Q2]), "operationType" : NewBodyOperationType.ADD, "depth" : 25 * mm, "offsetDistance" : 25 * mm});
        }
    });
